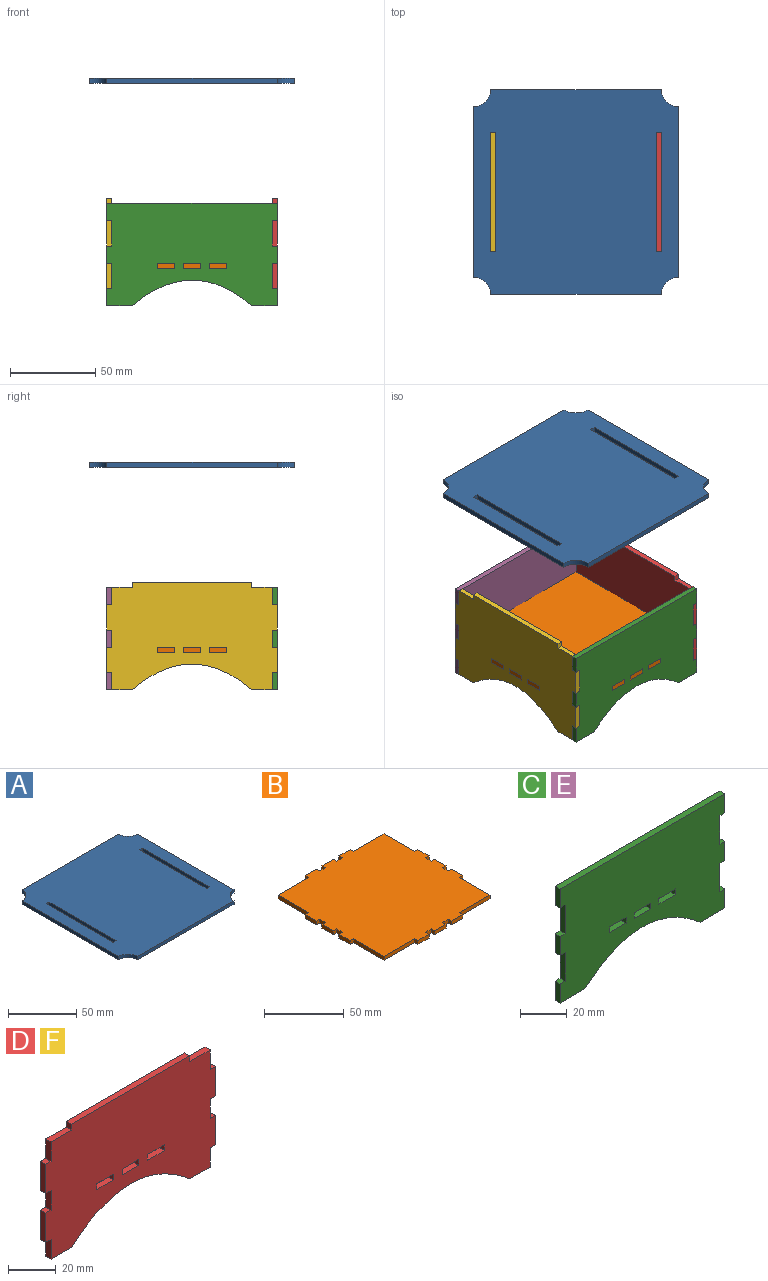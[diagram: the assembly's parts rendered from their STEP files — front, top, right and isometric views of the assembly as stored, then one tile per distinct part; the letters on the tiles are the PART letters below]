
ASSEMBLY  parts=6 mates=8
PART A: 18 faces, bbox 120x120x3 mm
  f0: plane 70x3mm, normal (-1,0,0), area 210mm2, adj f1,f11,f12,f13
  f1: plane 3x3mm, normal (0,1,0), area 9mm2, adj f0,f2,f12,f13
  f2: plane 70x3mm, normal (1,0,0), area 210mm2, adj f1,f11,f12,f13
  f3: plane 3x3mm, normal (0,1,0), area 9mm2, adj f4,f10,f12,f13
  f4: plane 70x3mm, normal (1,0,0), area 210mm2, adj f3,f5,f12,f13
  f5: plane 3x3mm, normal (0,-1,0), area 9mm2, adj f4,f10,f12,f13
  f6: plane 100x3mm, normal (0,1,0), area 300mm2, adj f12,f13,f14,f15
  f7: plane 100x3mm, normal (-1,0,0), area 300mm2, adj f12,f13,f14,f16
  f8: plane 100x3mm, normal (0,-1,0), area 300mm2, adj f12,f13,f16,f17
  f9: plane 100x3mm, normal (1,0,0), area 300mm2, adj f12,f13,f15,f17
  f10: plane 70x3mm, normal (-1,0,0), area 210mm2, adj f3,f5,f12,f13
  f11: plane 3x3mm, normal (0,-1,0), area 9mm2, adj f0,f2,f12,f13
  f12: plane 120x120mm, normal (0,0,1), area 13665.8mm2, adj f0,f1,f2,f3,f4,f5,f6,f7
  f13: plane 120x120mm, normal (0,0,-1), area 13665.8mm2, adj f0,f1,f2,f3,f4,f5,f6,f7
  f14: cylinder r=10mm len=10mm, axis (0,0,-1), area 47.1mm2, adj f6,f7,f12,f13
  f15: cylinder r=10mm len=10mm, axis (0,0,-1), area 47.1mm2, adj f6,f9,f12,f13
  f16: cylinder r=10mm len=10mm, axis (0,0,-1), area 47.1mm2, adj f7,f8,f12,f13
  f17: cylinder r=10mm len=10mm, axis (0,0,-1), area 47.1mm2, adj f8,f9,f12,f13
PART B: 54 faces, bbox 100x100x3 mm
  f0: plane 10x3mm, normal (0,1,0), area 30mm2, adj f1,f51,f52,f53
  f1: plane 3x3mm, normal (-1,0,0), area 9mm2, adj f0,f2,f52,f53
  f2: plane 5x3mm, normal (0,1,0), area 15mm2, adj f1,f3,f52,f53
  f3: plane 3x3mm, normal (1,0,0), area 9mm2, adj f2,f4,f52,f53
  f4: plane 10x3mm, normal (0,1,0), area 30mm2, adj f3,f5,f52,f53
  f5: plane 3x3mm, normal (-1,0,0), area 9mm2, adj f4,f6,f52,f53
  f6: plane 5x3mm, normal (0,1,0), area 15mm2, adj f5,f7,f52,f53
  f7: plane 3x3mm, normal (1,0,0), area 9mm2, adj f6,f8,f52,f53
  f8: plane 10x3mm, normal (0,1,0), area 30mm2, adj f7,f9,f52,f53
  f9: plane 3x3mm, normal (-1,0,0), area 9mm2, adj f8,f10,f52,f53
  f10: plane 27x3mm, normal (0,1,0), area 81mm2, adj f9,f11,f52,f53
  f11: plane 27x3mm, normal (-1,0,0), area 81mm2, adj f10,f12,f52,f53
  f12: plane 3x3mm, normal (0,1,0), area 9mm2, adj f11,f13,f52,f53
  f13: plane 10x3mm, normal (-1,0,0), area 30mm2, adj f12,f14,f52,f53
  f14: plane 3x3mm, normal (0,-1,0), area 9mm2, adj f13,f15,f52,f53
  f15: plane 5x3mm, normal (-1,0,0), area 15mm2, adj f14,f16,f52,f53
  f16: plane 3x3mm, normal (0,1,0), area 9mm2, adj f15,f17,f52,f53
  f17: plane 10x3mm, normal (-1,0,0), area 30mm2, adj f16,f18,f52,f53
  f18: plane 3x3mm, normal (0,-1,0), area 9mm2, adj f17,f19,f52,f53
  f19: plane 5x3mm, normal (-1,0,0), area 15mm2, adj f18,f20,f52,f53
  f20: plane 3x3mm, normal (0,1,0), area 9mm2, adj f19,f21,f52,f53
  f21: plane 10x3mm, normal (-1,0,0), area 30mm2, adj f20,f22,f52,f53
  f22: plane 3x3mm, normal (0,-1,0), area 9mm2, adj f21,f23,f52,f53
  f23: plane 27x3mm, normal (-1,0,0), area 81mm2, adj f22,f24,f52,f53
  f24: plane 27x3mm, normal (0,-1,0), area 81mm2, adj f23,f25,f52,f53
  f25: plane 3x3mm, normal (-1,0,0), area 9mm2, adj f24,f26,f52,f53
  f26: plane 10x3mm, normal (0,-1,0), area 30mm2, adj f25,f27,f52,f53
  f27: plane 3x3mm, normal (1,0,0), area 9mm2, adj f26,f28,f52,f53
  f28: plane 5x3mm, normal (0,-1,0), area 15mm2, adj f27,f29,f52,f53
  f29: plane 3x3mm, normal (-1,0,0), area 9mm2, adj f28,f30,f52,f53
  f30: plane 10x3mm, normal (0,-1,0), area 30mm2, adj f29,f31,f52,f53
  f31: plane 3x3mm, normal (1,0,0), area 9mm2, adj f30,f32,f52,f53
  f32: plane 5x3mm, normal (0,-1,0), area 15mm2, adj f31,f33,f52,f53
  f33: plane 3x3mm, normal (-1,0,0), area 9mm2, adj f32,f34,f52,f53
  f34: plane 10x3mm, normal (0,-1,0), area 30mm2, adj f33,f35,f52,f53
  f35: plane 3x3mm, normal (1,0,0), area 9mm2, adj f34,f36,f52,f53
  f36: plane 27x3mm, normal (0,-1,0), area 81mm2, adj f35,f37,f52,f53
  f37: plane 27x3mm, normal (1,0,0), area 81mm2, adj f36,f38,f52,f53
  f38: plane 3x3mm, normal (0,-1,0), area 9mm2, adj f37,f39,f52,f53
  f39: plane 10x3mm, normal (1,0,0), area 30mm2, adj f38,f40,f52,f53
  f40: plane 3x3mm, normal (0,1,0), area 9mm2, adj f39,f41,f52,f53
  f41: plane 5x3mm, normal (1,0,0), area 15mm2, adj f40,f42,f52,f53
  f42: plane 3x3mm, normal (0,-1,0), area 9mm2, adj f41,f43,f52,f53
  f43: plane 10x3mm, normal (1,0,0), area 30mm2, adj f42,f44,f52,f53
  f44: plane 3x3mm, normal (0,1,0), area 9mm2, adj f43,f45,f52,f53
  f45: plane 5x3mm, normal (1,0,0), area 15mm2, adj f44,f46,f52,f53
  f46: plane 3x3mm, normal (0,-1,0), area 9mm2, adj f45,f47,f52,f53
  f47: plane 10x3mm, normal (1,0,0), area 30mm2, adj f46,f48,f52,f53
  f48: plane 3x3mm, normal (0,1,0), area 9mm2, adj f47,f49,f52,f53
  f49: plane 27x3mm, normal (1,0,0), area 81mm2, adj f48,f50,f52,f53
  f50: plane 27x3mm, normal (0,1,0), area 81mm2, adj f49,f51,f52,f53
  f51: plane 3x3mm, normal (1,0,0), area 9mm2, adj f0,f50,f52,f53
  f52: plane 100x100mm, normal (0,0,1), area 9196mm2, adj f0,f1,f2,f3,f4,f5,f6,f7
  f53: plane 100x100mm, normal (0,0,-1), area 9196mm2, adj f0,f1,f2,f3,f4,f5,f6,f7
PART C: 36 faces, bbox 100x3x60 mm
  f0: plane 3x3mm, normal (1,0,0), area 9mm2, adj f1,f33,f34,f35
  f1: plane 10x3mm, normal (0,0,-1), area 30mm2, adj f0,f2,f34,f35
  f2: plane 3x3mm, normal (-1,0,0), area 9mm2, adj f1,f33,f34,f35
  f3: plane 3x3mm, normal (1,0,0), area 9mm2, adj f4,f30,f34,f35
  f4: plane 10x3mm, normal (0,0,-1), area 30mm2, adj f3,f5,f34,f35
  f5: plane 3x3mm, normal (-1,0,0), area 9mm2, adj f4,f30,f34,f35
  f6: plane 100x3mm, normal (0,0,1), area 300mm2, adj f7,f31,f34,f35
  f7: plane 10x3mm, normal (-1,0,0), area 30mm2, adj f6,f8,f34,f35
  f8: plane 3x3mm, normal (0,0,-1), area 9mm2, adj f7,f9,f34,f35
  f9: plane 15x3mm, normal (-1,0,0), area 45mm2, adj f8,f10,f34,f35
  f10: plane 3x3mm, normal (0,0,1), area 9mm2, adj f9,f11,f34,f35
  f11: plane 10x3mm, normal (-1,0,0), area 30mm2, adj f10,f12,f34,f35
  f12: plane 3x3mm, normal (0,0,-1), area 9mm2, adj f11,f13,f34,f35
  f13: plane 15x3mm, normal (-1,0,0), area 45mm2, adj f12,f14,f34,f35
  f14: plane 3x3mm, normal (0,0,1), area 9mm2, adj f13,f15,f34,f35
  f15: plane 10x3mm, normal (-1,0,0), area 30mm2, adj f14,f16,f34,f35
  f16: plane 15x3mm, normal (0,0,-1), area 45mm2, adj f15,f17,f34,f35
  f17: extruded ~70x15mm, area 233.4mm2, adj f16,f18,f34,f35
  f18: plane 15x3mm, normal (0,0,-1), area 45mm2, adj f17,f19,f34,f35
  f19: plane 10x3mm, normal (1,0,0), area 30mm2, adj f18,f20,f34,f35
  f20: plane 3x3mm, normal (0,0,1), area 9mm2, adj f19,f21,f34,f35
  f21: plane 15x3mm, normal (1,0,0), area 45mm2, adj f20,f22,f34,f35
  f22: plane 3x3mm, normal (0,0,-1), area 9mm2, adj f21,f23,f34,f35
  f23: plane 10x3mm, normal (1,0,0), area 30mm2, adj f22,f24,f34,f35
  f24: plane 3x3mm, normal (0,0,1), area 9mm2, adj f23,f25,f34,f35
  f25: plane 15x3mm, normal (1,0,0), area 45mm2, adj f24,f26,f34,f35
  f26: plane 3x3mm, normal (0,0,-1), area 9mm2, adj f25,f31,f34,f35
  f27: plane 3x3mm, normal (1,0,0), area 9mm2, adj f28,f32,f34,f35
  f28: plane 10x3mm, normal (0,0,-1), area 30mm2, adj f27,f29,f34,f35
  f29: plane 3x3mm, normal (-1,0,0), area 9mm2, adj f28,f32,f34,f35
  f30: plane 10x3mm, normal (0,0,1), area 30mm2, adj f3,f5,f34,f35
  f31: plane 10x3mm, normal (1,0,0), area 30mm2, adj f6,f26,f34,f35
  f32: plane 10x3mm, normal (0,0,1), area 30mm2, adj f27,f29,f34,f35
  f33: plane 10x3mm, normal (0,0,1), area 30mm2, adj f0,f2,f34,f35
  f34: plane 100x60mm, normal (0,-1,0), area 5030mm2, adj f0,f1,f2,f3,f4,f5,f6,f7
  f35: plane 100x60mm, normal (0,1,0), area 5030mm2, adj f0,f1,f2,f3,f4,f5,f6,f7
PART D: 40 faces, bbox 100x3x63 mm
  f0: plane 3x3mm, normal (1,0,0), area 9mm2, adj f1,f37,f38,f39
  f1: plane 10x3mm, normal (0,0,-1), area 30mm2, adj f0,f2,f38,f39
  f2: plane 3x3mm, normal (-1,0,0), area 9mm2, adj f1,f37,f38,f39
  f3: plane 3x3mm, normal (1,0,0), area 9mm2, adj f4,f34,f38,f39
  f4: plane 10x3mm, normal (0,0,-1), area 30mm2, adj f3,f5,f38,f39
  f5: plane 3x3mm, normal (-1,0,0), area 9mm2, adj f4,f34,f38,f39
  f6: plane 3x3mm, normal (1,0,0), area 9mm2, adj f7,f35,f38,f39
  f7: plane 10x3mm, normal (0,0,-1), area 30mm2, adj f6,f8,f38,f39
  f8: plane 3x3mm, normal (-1,0,0), area 9mm2, adj f7,f35,f38,f39
  f9: plane 3x3mm, normal (-1,0,0), area 9mm2, adj f10,f36,f38,f39
  f10: plane 12x3mm, normal (0,0,1), area 36mm2, adj f9,f11,f38,f39
  f11: plane 10x3mm, normal (-1,0,0), area 30mm2, adj f10,f12,f38,f39
  f12: plane 3x3mm, normal (0,0,1), area 9mm2, adj f11,f13,f38,f39
  f13: plane 15x3mm, normal (-1,0,0), area 45mm2, adj f12,f14,f38,f39
  f14: plane 3x3mm, normal (0,0,-1), area 9mm2, adj f13,f15,f38,f39
  f15: plane 10x3mm, normal (-1,0,0), area 30mm2, adj f14,f16,f38,f39
  f16: plane 3x3mm, normal (0,0,1), area 9mm2, adj f15,f17,f38,f39
  f17: plane 15x3mm, normal (-1,0,0), area 45mm2, adj f16,f18,f38,f39
  f18: plane 3x3mm, normal (0,0,-1), area 9mm2, adj f17,f19,f38,f39
  f19: plane 10x3mm, normal (-1,0,0), area 30mm2, adj f18,f20,f38,f39
  f20: plane 12x3mm, normal (0,0,-1), area 36mm2, adj f19,f21,f38,f39
  f21: extruded ~70x15mm, area 233.4mm2, adj f20,f22,f38,f39
  f22: plane 12x3mm, normal (0,0,-1), area 36mm2, adj f21,f23,f38,f39
  f23: plane 10x3mm, normal (1,0,0), area 30mm2, adj f22,f24,f38,f39
  f24: plane 3x3mm, normal (0,0,-1), area 9mm2, adj f23,f25,f38,f39
  f25: plane 15x3mm, normal (1,0,0), area 45mm2, adj f24,f26,f38,f39
  f26: plane 3x3mm, normal (0,0,1), area 9mm2, adj f25,f27,f38,f39
  f27: plane 10x3mm, normal (1,0,0), area 30mm2, adj f26,f28,f38,f39
  f28: plane 3x3mm, normal (0,0,-1), area 9mm2, adj f27,f29,f38,f39
  f29: plane 15x3mm, normal (1,0,0), area 45mm2, adj f28,f30,f38,f39
  f30: plane 3x3mm, normal (0,0,1), area 9mm2, adj f29,f31,f38,f39
  f31: plane 10x3mm, normal (1,0,0), area 30mm2, adj f30,f32,f38,f39
  f32: plane 12x3mm, normal (0,0,1), area 36mm2, adj f31,f33,f38,f39
  f33: plane 3x3mm, normal (1,0,0), area 9mm2, adj f32,f36,f38,f39
  f34: plane 10x3mm, normal (0,0,1), area 30mm2, adj f3,f5,f38,f39
  f35: plane 10x3mm, normal (0,0,1), area 30mm2, adj f6,f8,f38,f39
  f36: plane 70x3mm, normal (0,0,1), area 210mm2, adj f9,f33,f38,f39
  f37: plane 10x3mm, normal (0,0,1), area 30mm2, adj f0,f2,f38,f39
  f38: plane 100x63mm, normal (0,-1,0), area 5240mm2, adj f0,f1,f2,f3,f4,f5,f6,f7
  f39: plane 100x63mm, normal (0,1,0), area 5240mm2, adj f0,f1,f2,f3,f4,f5,f6,f7
PART E: same geometry as C
PART F: same geometry as D
PLACE A t=(4.24,1.15,104.89)mm
PLACE B t=(4.24,1.15,-3.45)mm fixed
PLACE C t=(4.24,-45.85,4.55)mm
PLACE D rot(axis=(0,0,1),90deg) t=(51.24,1.15,4.55)mm
PLACE E t=(4.24,51.15,4.55)mm
PLACE F rot(axis=(0,0,1),90deg) t=(-45.76,1.15,4.55)mm
MATE planar C.f1 <-> B.f52  axis (0,0,-1) through (4.24,-47.35,-0.45)mm
MATE planar C.f3 <-> B.f25  axis (1,0,0) through (-15.76,-47.35,-1.95)mm
MATE planar A.f2 <-> D.f39  axis (1,0,0) through (51.24,1.15,104.89)mm
MATE planar D.f35 <-> B.f53  axis (0,0,1) through (52.74,16.15,-3.45)mm
MATE planar B.f24 <-> C.f35  axis (0,-1,0) through (-29.26,-45.85,-1.95)mm
MATE planar D.f3 <-> B.f38  axis (0,1,0) through (51.24,-18.85,-1.95)mm
MATE planar D.f39 <-> B.f37  axis (-1,0,0) through (51.24,1.15,9.13)mm
MATE planar A.f11 <-> D.f33  axis (0,-1,0) through (52.74,36.15,106.39)mm
